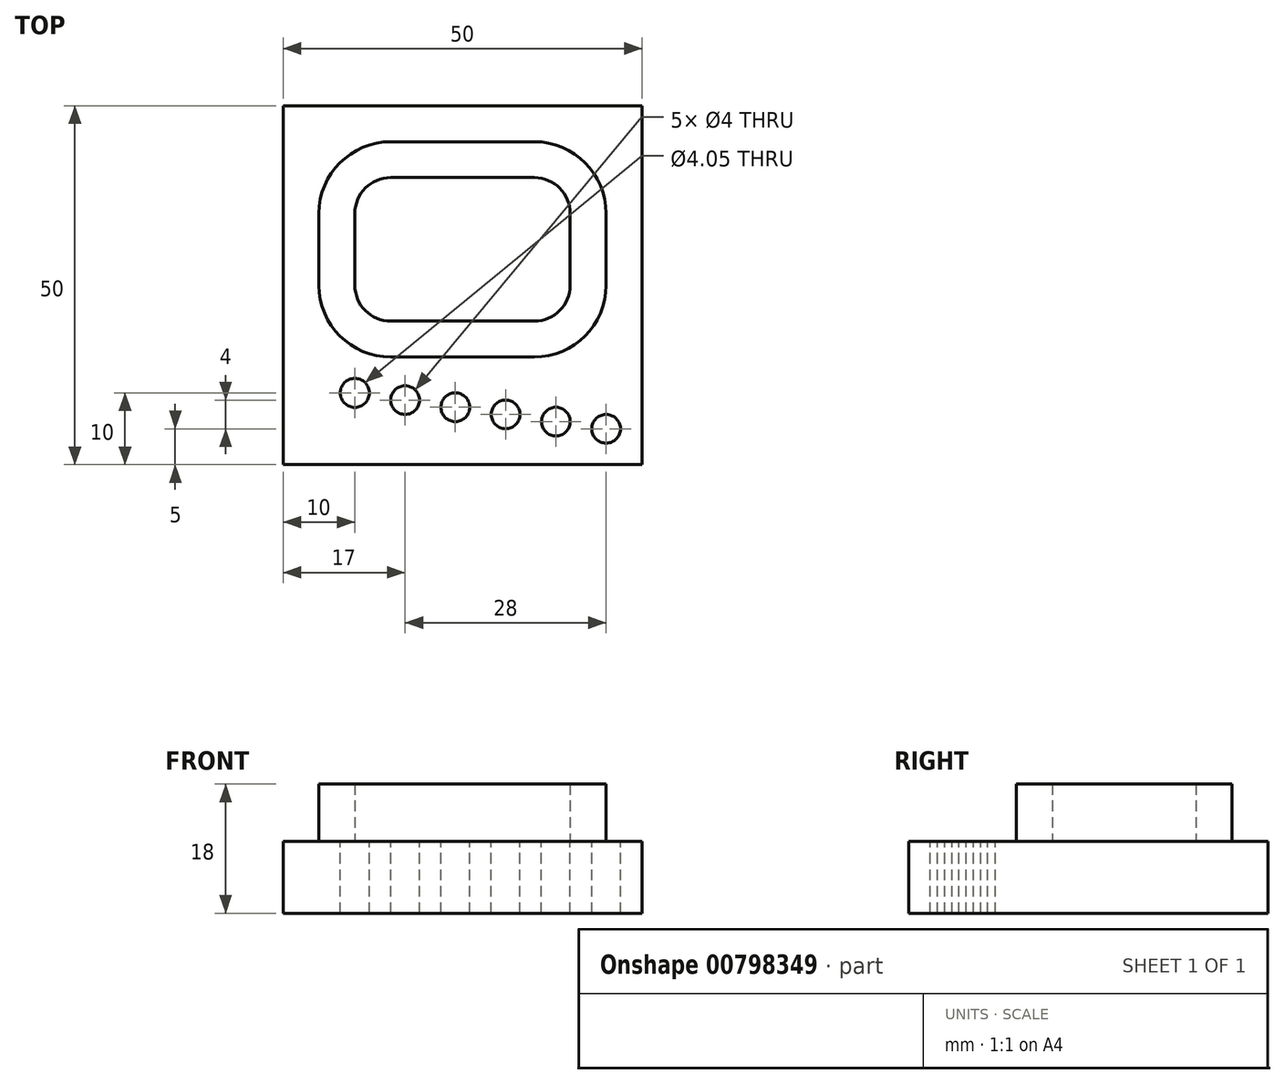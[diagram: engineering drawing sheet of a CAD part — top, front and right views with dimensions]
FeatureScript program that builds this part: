
annotation { "Feature Type Name" : "Feature", "Feature Type Description" : "" }
export const myFeature = defineFeature(function(context is Context, id is Id, definition is map)
    precondition{}
    {
        {
            var Q0;
            Q0=qCreatedBy(makeId("Top.planeOp"),FACE);
            var sketch = newSketch(context, id + "F0", { "sketchPlane" : qUnion([Q0])});
            skLineSegment(sketch, "E0.bottom", {"start": v(0, 0) * mm, "end": v(50, 0) * mm});
            skLineSegment(sketch, "E0.top", {"start": v(0, 50) * mm, "end": v(50, 50) * mm});
            skLineSegment(sketch, "E0.left", {"start": v(0, 0) * mm, "end": v(0, 50) * mm});
            skLineSegment(sketch, "E0.right", {"start": v(50, 0) * mm, "end": v(50, 50) * mm});
            skSolve(sketch);
        }
        {
            var Q0;
            Q0=makeQuery(id+"F0.imprint","IMPRINT",FACE,{"disambiguationData":[TD([[makeQuery(id+"F0.imprint","IMPRINT",EDGE,{"derivedFrom":sQuery(id+"F0.wireOp",EDGE,"E0.bottom")}),1.0]])]});
            extrude(context, id + "F1", {"entities" : qUnion([Q0]), "depth" : 10 * mm, "offsetDistance" : 25 * mm});
        }
        {
            var Q0;
            Q0=makeQuery(id+"F1.opExtrude","CAP_FACE",FACE,{"disambiguationData":[OSD([sQuery(id+"F0.wireOp",EDGE,"E0.bottom"),sQuery(id+"F0.wireOp",EDGE,"E0.top"),sQuery(id+"F0.wireOp",EDGE,"E0.left"),sQuery(id+"F0.wireOp",EDGE,"E0.right")])],"isStart":false});
            var sketch = newSketch(context, id + "F2", { "sketchPlane" : qUnion([Q0])});
            skLineSegment(sketch, "E1.bottom", {"start": v(15, 45) * mm, "end": v(35, 45) * mm});
            skLineSegment(sketch, "E1.top", {"start": v(15, 15) * mm, "end": v(35, 15) * mm});
            skLineSegment(sketch, "E1.left", {"start": v(5, 35) * mm, "end": v(5, 25) * mm});
            skLineSegment(sketch, "E1.right", {"start": v(45, 35) * mm, "end": v(45, 25) * mm});
            skLineSegment(sketch, "E2.bottom", {"start": v(15, 40) * mm, "end": v(35, 40) * mm});
            skLineSegment(sketch, "E2.top", {"start": v(15, 20) * mm, "end": v(35, 20) * mm});
            skLineSegment(sketch, "E2.left", {"start": v(10, 35) * mm, "end": v(10, 25) * mm});
            skLineSegment(sketch, "E2.right", {"start": v(40, 35) * mm, "end": v(40, 25) * mm});
            skPoint(sketch, "E3", {"position": v(25, 20) * mm});
            skPoint(sketch, "E4", {"position": v(25, 15) * mm});
            skPoint(sketch, "E5", {"position": v(40, 30) * mm});
            skPoint(sketch, "E6", {"position": v(45, 30) * mm});
            skPoint(sketch, "E7", {"position": v(25, 0) * mm});
            skPoint(sketch, "E8.visualSharp", {"position": v(10, 40) * mm});
            skArc(sketch, "E8.filletArc", {"start": v(15, 40) * mm, "mid": v(11.46, 38.54) * mm, "end": v(10, 35) * mm});
            skPoint(sketch, "E9.visualSharp", {"position": v(10, 20) * mm});
            skArc(sketch, "E9.filletArc", {"start": v(10, 25) * mm, "mid": v(11.46, 21.46) * mm, "end": v(15, 20) * mm});
            skPoint(sketch, "E10.visualSharp", {"position": v(40, 20) * mm});
            skArc(sketch, "E10.filletArc", {"start": v(35, 20) * mm, "mid": v(38.54, 21.46) * mm, "end": v(40, 25) * mm});
            skPoint(sketch, "E11.visualSharp", {"position": v(40, 40) * mm});
            skArc(sketch, "E11.filletArc", {"start": v(40, 35) * mm, "mid": v(38.54, 38.54) * mm, "end": v(35, 40) * mm});
            skPoint(sketch, "E12.visualSharp", {"position": v(5, 45) * mm});
            skArc(sketch, "E12.filletArc", {"start": v(15, 45) * mm, "mid": v(7.93, 42.07) * mm, "end": v(5, 35) * mm});
            skPoint(sketch, "E13.visualSharp", {"position": v(5, 15) * mm});
            skArc(sketch, "E13.filletArc", {"start": v(5, 25) * mm, "mid": v(7.93, 17.93) * mm, "end": v(15, 15) * mm});
            skPoint(sketch, "E14.visualSharp", {"position": v(45, 15) * mm});
            skArc(sketch, "E14.filletArc", {"start": v(35, 15) * mm, "mid": v(42.07, 17.93) * mm, "end": v(45, 25) * mm});
            skPoint(sketch, "E15.visualSharp", {"position": v(45, 45) * mm});
            skArc(sketch, "E15.filletArc", {"start": v(45, 35) * mm, "mid": v(42.07, 42.07) * mm, "end": v(35, 45) * mm});
            skSolve(sketch);
        }
        {
            var Q0;
            Q0=makeQuery(id+"F2.imprint","IMPRINT",FACE,{"disambiguationData":[TD([[makeQuery(id+"F2.imprint","IMPRINT",EDGE,{"derivedFrom":sQuery(id+"F2.wireOp",EDGE,"E1.bottom")}),-1.0]])]});
            extrude(context, id + "F3", {"entities" : qUnion([Q0]), "operationType" : NewBodyOperationType.ADD, "depth" : 8 * mm, "offsetDistance" : 25 * mm});
        }
        {
            var Q0;
            {var subQ0=sQuery(id+"F0.wireOp",EDGE,"E0.left");var subQ1=sQuery(id+"F0.wireOp",EDGE,"E0.bottom");var subQ2=sQuery(id+"F0.wireOp",EDGE,"E0.right");var subQ3=sQuery(id+"F0.wireOp",EDGE,"E0.top");Q0=makeQuery(id+"F3.boolean.opBoolean","SPLIT",FACE,{"disambiguationData":[TD([makeQuery(id+"F1.opExtrude","SWEPT_FACE",FACE,{"disambiguationData":[OSD([subQ1])]})])],"derivedFrom":makeQuery(id+"F1.opExtrude","CAP_FACE",FACE,{"disambiguationData":[OSD([subQ1,subQ3,subQ0,subQ2])],"isStart":false})});}
            var sketch = newSketch(context, id + "F4", { "sketchPlane" : qUnion([Q0])});
            skCircle(sketch, "E16", {"center": v(10, 10) * mm, "radius": 2.03 * mm});
            skCircle(sketch, "E17", {"center": v(17, 9) * mm, "radius": 2 * mm});
            skCircle(sketch, "E18", {"center": v(24, 8) * mm, "radius": 2 * mm});
            skCircle(sketch, "E19", {"center": v(31, 7) * mm, "radius": 2 * mm});
            skCircle(sketch, "E20", {"center": v(38, 6) * mm, "radius": 2 * mm});
            skCircle(sketch, "E21", {"center": v(45, 5) * mm, "radius": 2 * mm});
            skSolve(sketch);
        }
        {
            var Q0;
            Q0=makeQuery(id+"F4.imprint","IMPRINT",FACE,{"disambiguationData":[TD([[makeQuery(id+"F4.imprint","IMPRINT",EDGE,{"derivedFrom":sQuery(id+"F4.wireOp",EDGE,"E16")}),1.0]])]});
            var Q1;
            Q1=makeQuery(id+"F4.imprint","IMPRINT",FACE,{"disambiguationData":[TD([[makeQuery(id+"F4.imprint","IMPRINT",EDGE,{"derivedFrom":sQuery(id+"F4.wireOp",EDGE,"E17")}),1.0]])]});
            var Q2;
            Q2=makeQuery(id+"F4.imprint","IMPRINT",FACE,{"disambiguationData":[TD([[makeQuery(id+"F4.imprint","IMPRINT",EDGE,{"derivedFrom":sQuery(id+"F4.wireOp",EDGE,"E18")}),1.0]])]});
            var Q3;
            Q3=makeQuery(id+"F4.imprint","IMPRINT",FACE,{"disambiguationData":[TD([[makeQuery(id+"F4.imprint","IMPRINT",EDGE,{"derivedFrom":sQuery(id+"F4.wireOp",EDGE,"E19")}),1.0]])]});
            var Q4;
            Q4=makeQuery(id+"F4.imprint","IMPRINT",FACE,{"disambiguationData":[TD([[makeQuery(id+"F4.imprint","IMPRINT",EDGE,{"derivedFrom":sQuery(id+"F4.wireOp",EDGE,"E20")}),1.0]])]});
            var Q5;
            Q5=makeQuery(id+"F4.imprint","IMPRINT",FACE,{"disambiguationData":[TD([[makeQuery(id+"F4.imprint","IMPRINT",EDGE,{"derivedFrom":sQuery(id+"F4.wireOp",EDGE,"E21")}),1.0]])]});
            extrude(context, id + "F5", {"entities" : qUnion([Q0, Q1, Q2, Q3, Q4, Q5]), "operationType" : NewBodyOperationType.REMOVE, "oppositeDirection" : true, "depth" : 25 * mm, "offsetDistance" : 25 * mm});
        }
    });
